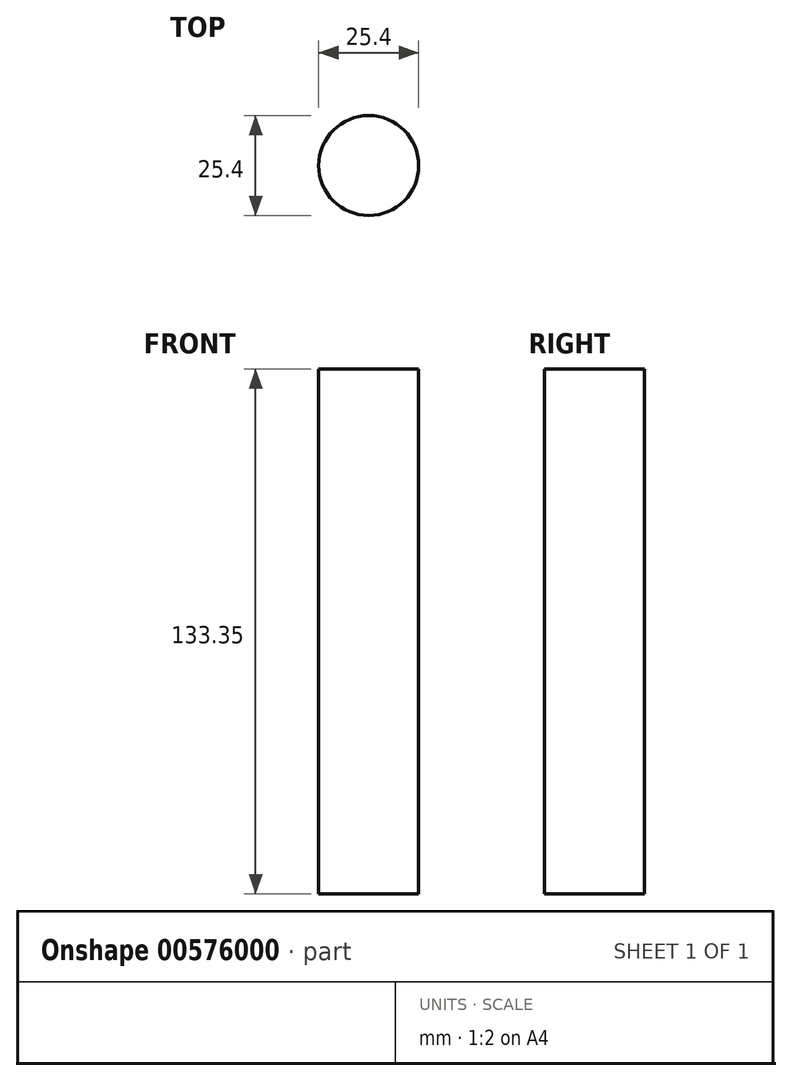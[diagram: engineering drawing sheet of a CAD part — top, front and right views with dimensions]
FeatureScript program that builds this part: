
annotation { "Feature Type Name" : "Feature", "Feature Type Description" : "" }
export const myFeature = defineFeature(function(context is Context, id is Id, definition is map)
    precondition{}
    {
        {
            var Q0;
            Q0=qCreatedBy(makeId("Top.planeOp"),FACE);
            var sketch = newSketch(context, id + "F0", { "sketchPlane" : qUnion([Q0])});
            skCircle(sketch, "E0", {"center": v(0, 1.03) * mm, "radius": 12.7 * mm});
            skSolve(sketch);
        }
        {
            var Q0;
            Q0 = qSketchRegion(id + "F0", true);
            extrude(context, id + "F1", {"entities" : qUnion([Q0]), "depth" : 133.35 * mm, "offsetDistance" : 25.4 * mm});
        }
    });
